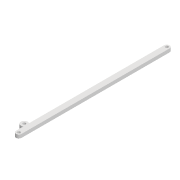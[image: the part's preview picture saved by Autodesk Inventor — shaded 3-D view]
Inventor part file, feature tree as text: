
AUTODESK INVENTOR PART (.ipt)
format: ipt  version: 2022 (Build 260153000, 153)  size: 95,232 bytes
history: native  units: mm
features: extrude x1, sketch x1
ambient origin geometry x8: Origin, YZ Plane, XZ Plane, XY Plane, X Axis, Y Axis, Z Axis, Center Point
bodies: Solid1 (feature_tree)
feature tree (2):
  extrude  "Extrusion1"  Depth=8.0mm
  sketch  "Sketch1"  dims[d0=215.0mm d1=8.0mm d2=4.2mm d3=4.2mm d4=5.0mm d5=0.0mm d6=4.2mm d7=10.0mm d8=3.0mm d9=15.0mm]
